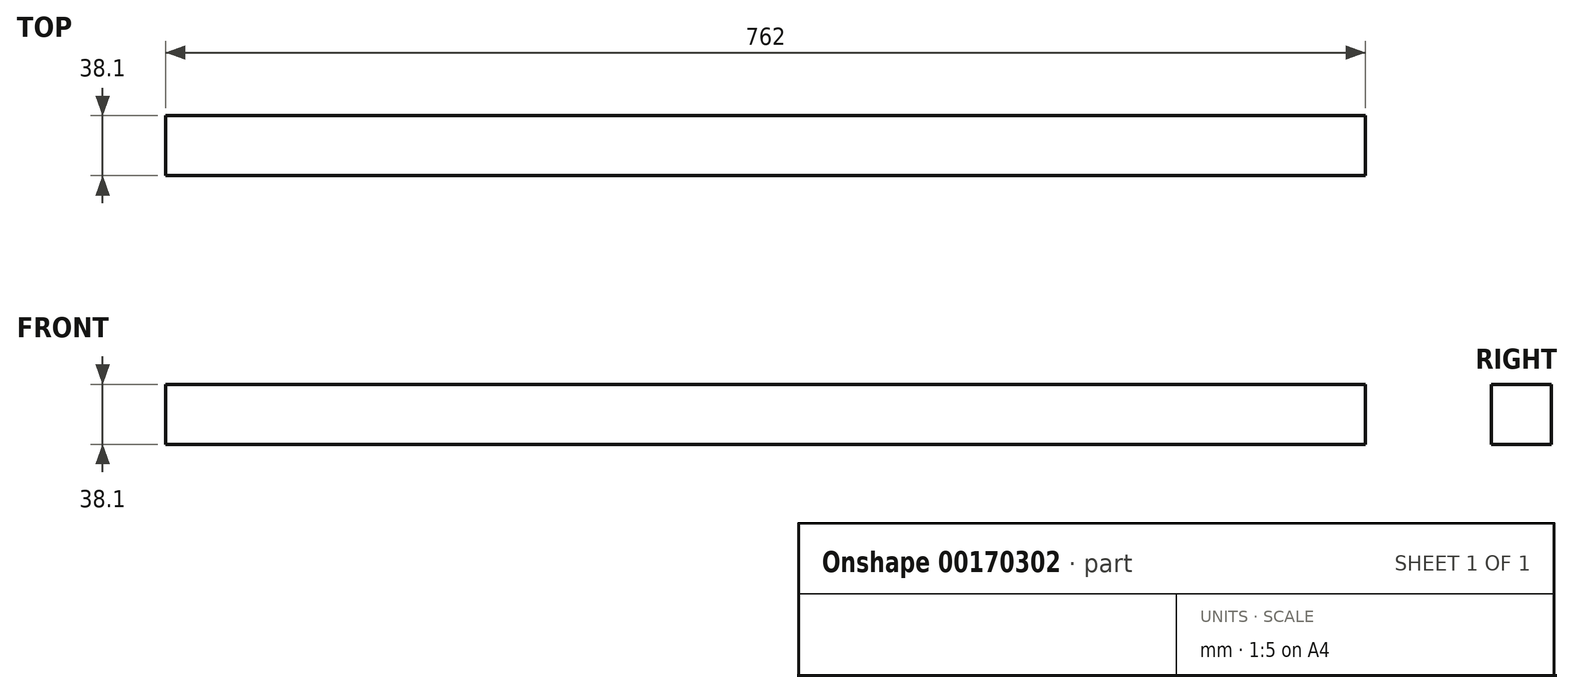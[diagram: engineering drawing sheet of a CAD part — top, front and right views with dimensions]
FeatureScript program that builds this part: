
annotation { "Feature Type Name" : "Feature", "Feature Type Description" : "" }
export const myFeature = defineFeature(function(context is Context, id is Id, definition is map)
    precondition{}
    {
        {
            var Q0;
            Q0=qCreatedBy(makeId("Top.planeOp"),FACE);
            var sketch = newSketch(context, id + "F0", { "sketchPlane" : qUnion([Q0])});
            skLineSegment(sketch, "E0.bottom", {"start": v(-373.3, 19.05) * mm, "end": v(388.7, 19.05) * mm});
            skLineSegment(sketch, "E0.top", {"start": v(-373.3, -19.05) * mm, "end": v(388.7, -19.05) * mm});
            skLineSegment(sketch, "E0.left", {"start": v(-373.3, 19.05) * mm, "end": v(-373.3, -19.05) * mm});
            skLineSegment(sketch, "E0.right", {"start": v(388.7, 19.05) * mm, "end": v(388.7, -19.05) * mm});
            skPoint(sketch, "E0.middle", {"position": v(7.7, 0) * mm});
            skSolve(sketch);
        }
        {
            var Q0;
            Q0=makeQuery(id+"F0.imprint","IMPRINT",FACE,{"disambiguationData":[TD([[makeQuery(id+"F0.imprint","IMPRINT",EDGE,{"derivedFrom":sQuery(id+"F0.wireOp",EDGE,"E0.bottom")}),-1.0]])]});
            extrude(context, id + "F1", {"entities" : qUnion([Q0]), "depth" : 38.1 * mm});
        }
    });
